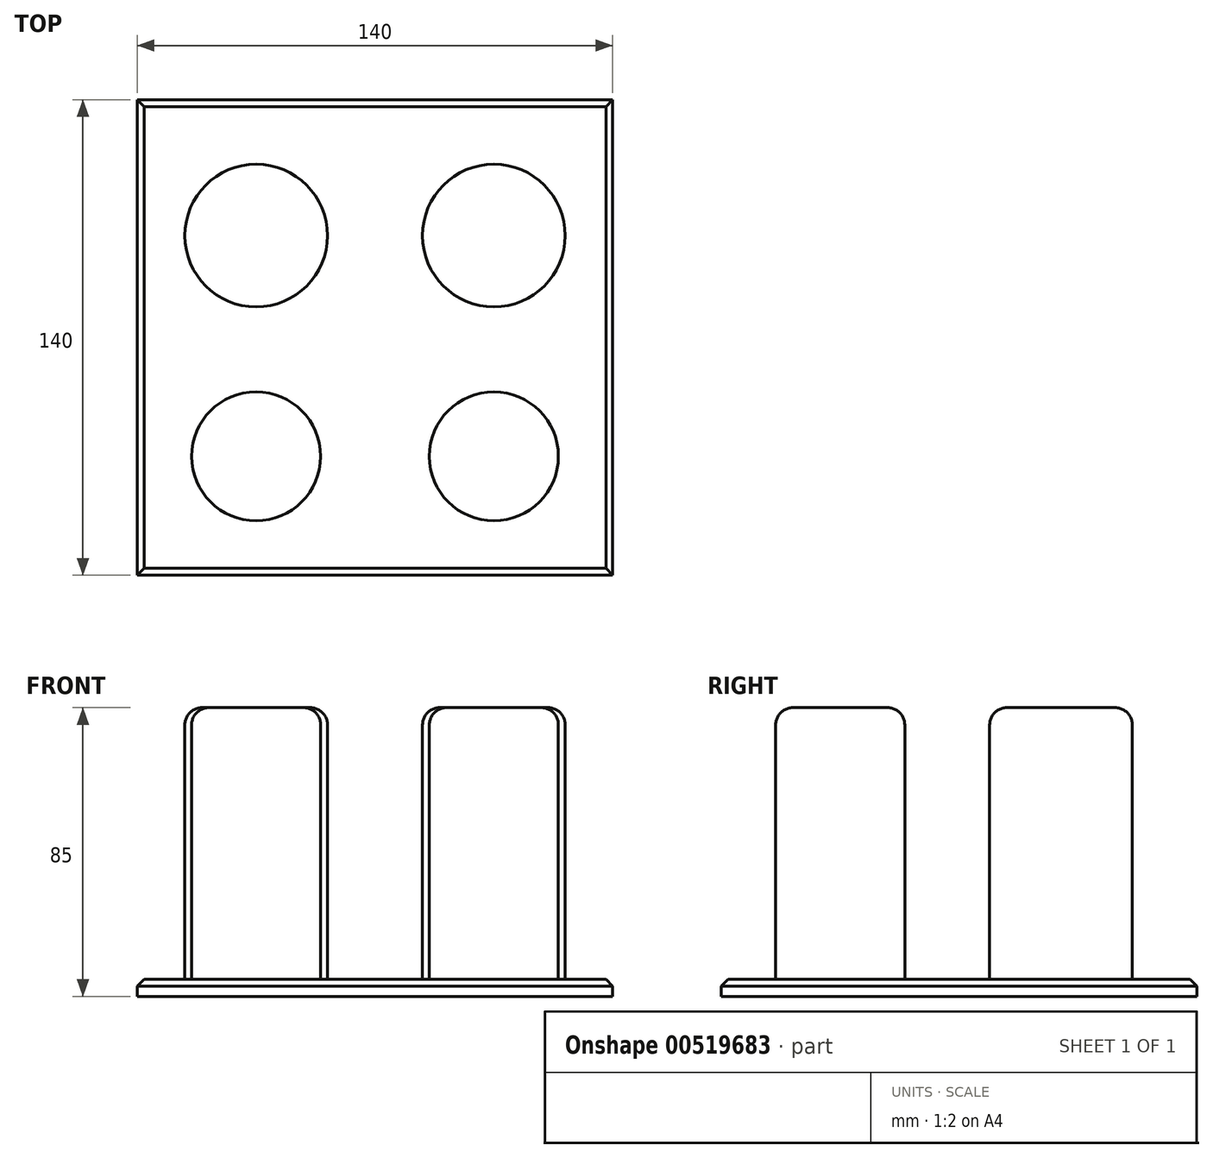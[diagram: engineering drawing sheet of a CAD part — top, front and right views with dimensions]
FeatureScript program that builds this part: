
annotation { "Feature Type Name" : "Feature", "Feature Type Description" : "" }
export const myFeature = defineFeature(function(context is Context, id is Id, definition is map)
    precondition{}
    {
        {
            var Q0;
            Q0=qCreatedBy(makeId("Top.planeOp"),FACE);
            var sketch = newSketch(context, id + "F0", { "sketchPlane" : qUnion([Q0])});
            skLineSegment(sketch, "E0.bottom", {"start": v(70, -70) * mm, "end": v(-70, -70) * mm});
            skLineSegment(sketch, "E0.top", {"start": v(70, 70) * mm, "end": v(-70, 70) * mm});
            skLineSegment(sketch, "E0.left", {"start": v(70, -70) * mm, "end": v(70, 70) * mm});
            skLineSegment(sketch, "E0.right", {"start": v(-70, -70) * mm, "end": v(-70, 70) * mm});
            skPoint(sketch, "E0.middle", {"position": v(0, 0) * mm});
            skSolve(sketch);
        }
        {
            var Q0;
            Q0=makeQuery(id+"F0.imprint","IMPRINT",FACE,{"disambiguationData":[TD([[makeQuery(id+"F0.imprint","IMPRINT",EDGE,{"derivedFrom":sQuery(id+"F0.wireOp",EDGE,"E0.bottom")}),-1.0]])]});
            extrude(context, id + "F1", {"entities" : qUnion([Q0]), "depth" : 5 * mm, "offsetDistance" : 25 * mm});
        }
        {
            var Q0;
            Q0=makeQuery(id+"F1.opExtrude","CAP_EDGE",EDGE,{"disambiguationData":[OSD([sQuery(id+"F0.wireOp",EDGE,"E0.bottom")])],"isStart":false});
            var Q1;
            Q1=makeQuery(id+"F1.opExtrude","CAP_EDGE",EDGE,{"disambiguationData":[OSD([sQuery(id+"F0.wireOp",EDGE,"E0.top")])],"isStart":false});
            var Q2;
            Q2=makeQuery(id+"F1.opExtrude","CAP_EDGE",EDGE,{"disambiguationData":[OSD([sQuery(id+"F0.wireOp",EDGE,"E0.right")])],"isStart":false});
            var Q3;
            Q3=makeQuery(id+"F1.opExtrude","CAP_EDGE",EDGE,{"disambiguationData":[OSD([sQuery(id+"F0.wireOp",EDGE,"E0.left")])],"isStart":false});
            chamfer(context, id + "F2", {"entities" : qUnion([Q0, Q1, Q2, Q3]), "width" : 2 * mm, "tangentPropagation" : true});
        }
        {
            var Q0;
            Q0=makeQuery(id+"F1.opExtrude","CAP_FACE",FACE,{"disambiguationData":[OSD([sQuery(id+"F0.wireOp",EDGE,"E0.bottom"),sQuery(id+"F0.wireOp",EDGE,"E0.top"),sQuery(id+"F0.wireOp",EDGE,"E0.left"),sQuery(id+"F0.wireOp",EDGE,"E0.right")])],"isStart":false});
            var sketch = newSketch(context, id + "F3", { "sketchPlane" : qUnion([Q0])});
            skCircle(sketch, "E1", {"center": v(-35, 30) * mm, "radius": 21 * mm});
            skCircle(sketch, "E2", {"center": v(35, 30) * mm, "radius": 21 * mm});
            skCircle(sketch, "E3", {"center": v(-35, -35) * mm, "radius": 19 * mm});
            skCircle(sketch, "E4", {"center": v(35, -35) * mm, "radius": 19 * mm});
            skLineSegment(sketch, "E5", {"start": v(-92.25, 30) * mm, "end": v(134.42, 30) * mm, "construction": true});
            skLineSegment(sketch, "E6", {"start": v(-99.82, -35) * mm, "end": v(117.84, -35) * mm, "construction": true});
            skSolve(sketch);
        }
        {
            var Q0;
            Q0 = qSketchRegion(id + "F3", true);
            extrude(context, id + "F4", {"entities" : qUnion([Q0]), "operationType" : NewBodyOperationType.ADD, "depth" : 80 * mm, "offsetDistance" : 25 * mm});
        }
        {
            var Q0;
            Q0=makeQuery(id+"F4.opExtrude","CAP_EDGE",EDGE,{"disambiguationData":[OSD([sQuery(id+"F3.wireOp",EDGE,"E1")])],"isStart":false});
            var Q1;
            Q1=makeQuery(id+"F4.opExtrude","CAP_EDGE",EDGE,{"disambiguationData":[OSD([sQuery(id+"F3.wireOp",EDGE,"E2")])],"isStart":false});
            var Q2;
            Q2=makeQuery(id+"F4.opExtrude","CAP_EDGE",EDGE,{"disambiguationData":[OSD([sQuery(id+"F3.wireOp",EDGE,"E3")])],"isStart":false});
            var Q3;
            Q3=makeQuery(id+"F4.opExtrude","CAP_EDGE",EDGE,{"disambiguationData":[OSD([sQuery(id+"F3.wireOp",EDGE,"E4")])],"isStart":false});
            fillet(context, id + "F5", {"entities" : qUnion([Q0, Q1, Q2, Q3]), "radius" : 5 * mm, "tangentPropagation" : true, "allowEdgeOverflow" : false});
        }
    });
